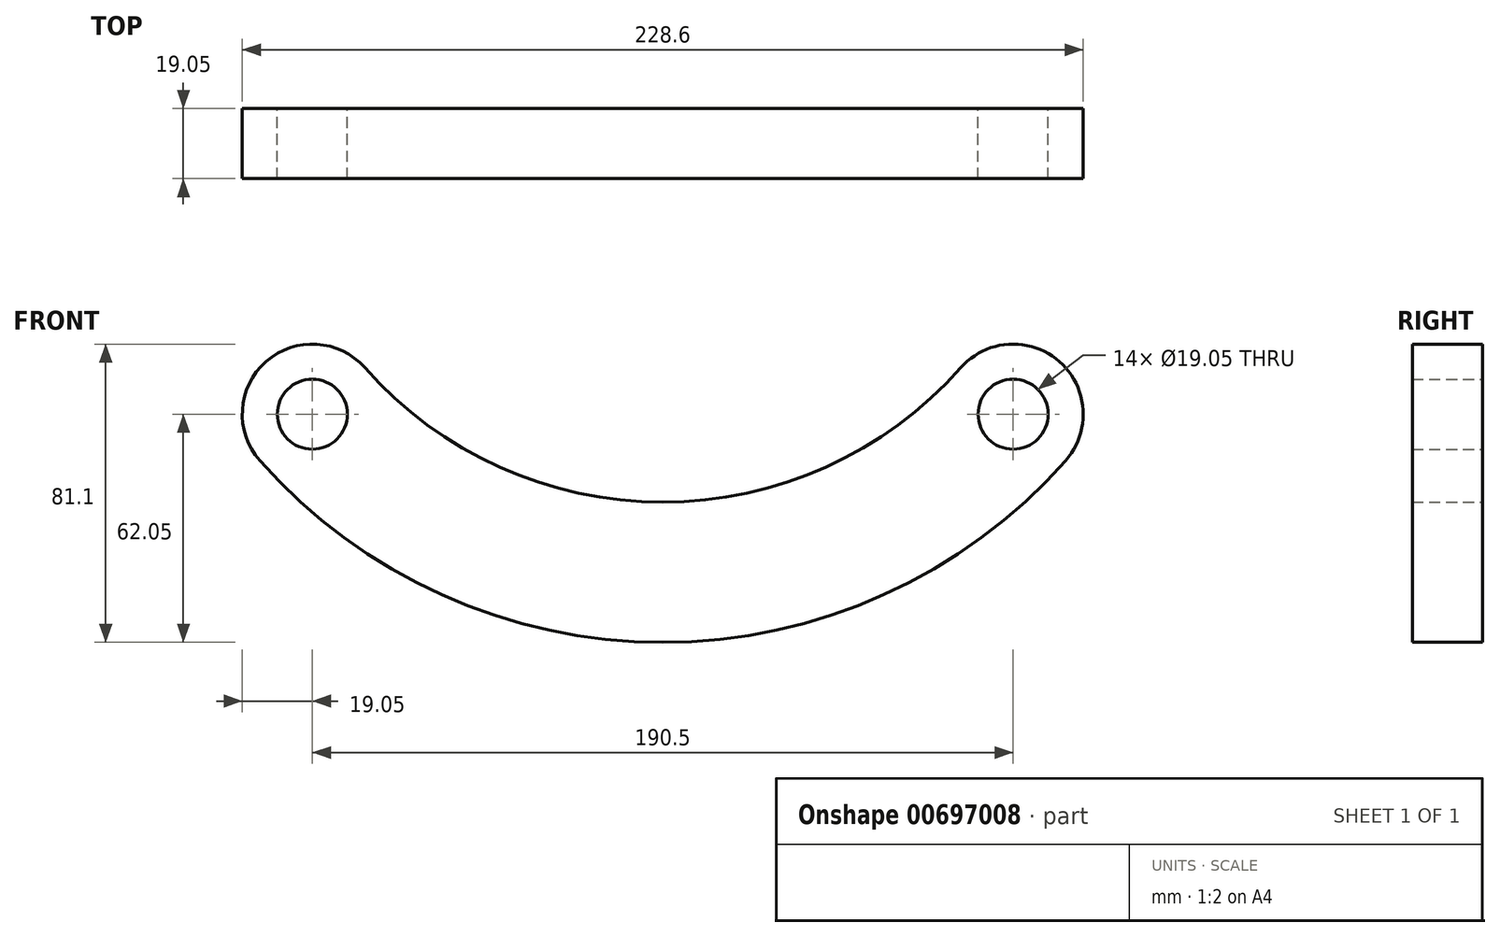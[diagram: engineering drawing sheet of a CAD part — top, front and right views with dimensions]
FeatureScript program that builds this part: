
annotation { "Feature Type Name" : "Feature", "Feature Type Description" : "" }
export const myFeature = defineFeature(function(context is Context, id is Id, definition is map)
    precondition{}
    {
        {
            var Q0;
            Q0=qCreatedBy(makeId("Front.planeOp"),FACE);
            var sketch = newSketch(context, id + "F0", { "sketchPlane" : qUnion([Q0])});
            skCircle(sketch, "E0", {"center": v(0, 0) * mm, "radius": 9.53 * mm});
            skCircle(sketch, "E1", {"center": v(190.5, 0) * mm, "radius": 9.53 * mm});
            skArc(sketch, "E2", {"start": v(-14.29, -12.6) * mm, "mid": v(95.25, -62.05) * mm, "end": v(204.79, -12.6) * mm});
            skArc(sketch, "E3", {"start": v(14.29, 12.6) * mm, "mid": v(-12.6, 14.29) * mm, "end": v(-14.29, -12.6) * mm});
            skArc(sketch, "E4", {"start": v(204.79, -12.6) * mm, "mid": v(203.1, 14.29) * mm, "end": v(176.21, 12.6) * mm});
            skArc(sketch, "E5", {"start": v(14.29, 12.6) * mm, "mid": v(95.25, -23.95) * mm, "end": v(176.21, 12.6) * mm});
            skSolve(sketch);
        }
        {
            var Q0;
            Q0=makeQuery(id+"F0.imprint","IMPRINT",FACE,{"disambiguationData":[TD([[makeQuery(id+"F0.imprint","IMPRINT",EDGE,{"derivedFrom":sQuery(id+"F0.wireOp",EDGE,"E0")}),-1.0]])]});
            extrude(context, id + "F1", {"entities" : qUnion([Q0]), "depth" : 19.05 * mm});
        }
    });
